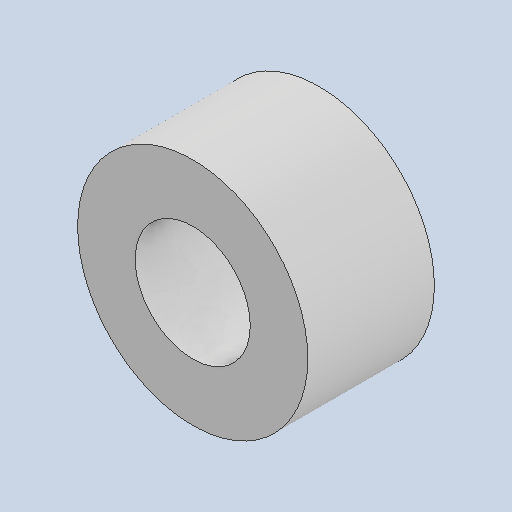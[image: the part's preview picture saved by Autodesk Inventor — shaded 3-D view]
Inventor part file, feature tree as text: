
AUTODESK INVENTOR PART (.ipt)
format: ipt  version: 2024.3 (Build 283343000, 343)  size: 211,968 bytes
history: native  units: mm
features: other x1, extrude x1, sketch x1
ambient origin geometry x8: Origin, YZ Plane, XZ Plane, XY Plane, X Axis, Y Axis, Z Axis, Center Point
bodies: Body1 (feature_tree)
feature tree (3):
  other  "ソリッド1"
  extrude  "押し出し1"  Depth=5.0mm
  sketch  "スケッチ1"
